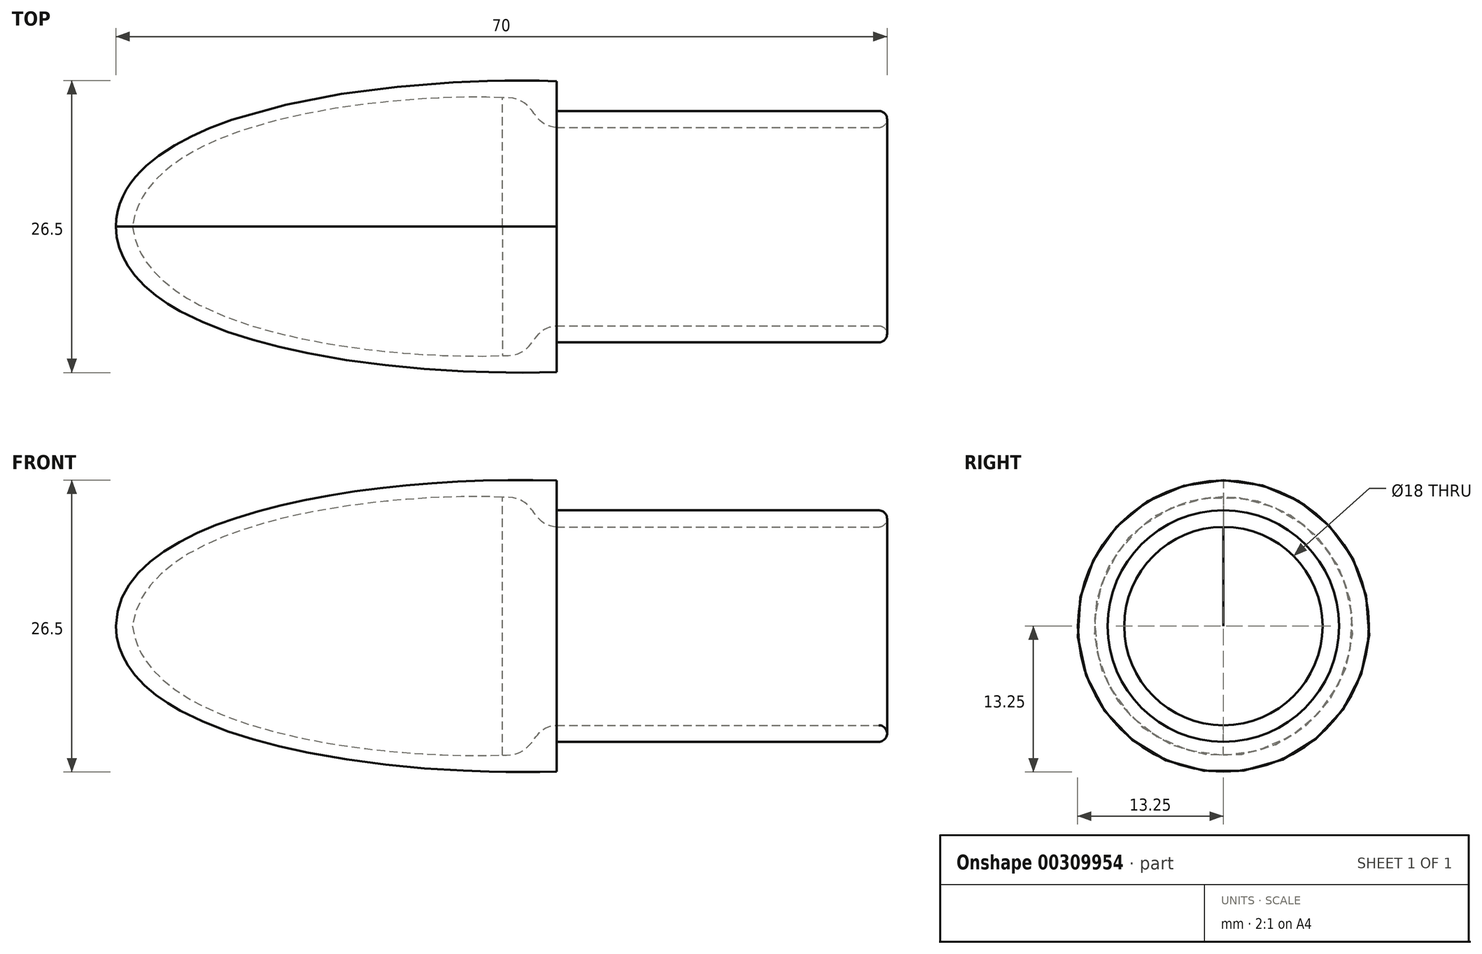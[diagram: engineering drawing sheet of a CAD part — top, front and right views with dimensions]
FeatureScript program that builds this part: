
annotation { "Feature Type Name" : "Feature", "Feature Type Description" : "" }
export const myFeature = defineFeature(function(context is Context, id is Id, definition is map)
    precondition{}
    {
        {
            var Q0;
            Q0=qCreatedBy(makeId("Front.planeOp"),FACE);
            var sketch = newSketch(context, id + "F0", { "sketchPlane" : qUnion([Q0])});
            skLineSegment(sketch, "E0", {"start": v(0, 10.5) * mm, "end": v(0, 13.2) * mm});
            skLineSegment(sketch, "E1", {"start": v(0, 10.5) * mm, "end": v(29.25, 10.5) * mm});
            skLineSegment(sketch, "E2", {"start": v(30, 9.75) * mm, "end": v(30, 9.75) * mm});
            skLineSegment(sketch, "E3", {"start": v(29.25, 9) * mm, "end": v(0, 9) * mm});
            skFitSpline(sketch, "E4", {"points": [v(0, 13.2) * mm, v(-40, 0) * mm], "startDerivative": vector(-48.79, 1.48) * mm, "endDerivative": vector(-0.4, -31.35) * mm});
            skLineSegment(sketch, "E5", {"start": v(-40, 0) * mm, "end": v(-38.5, 0) * mm});
            skLineSegment(sketch, "E6", {"start": v(0, 0) * mm, "end": v(-68.39, 0) * mm, "construction": true});
            skPoint(sketch, "E7.visualSharp", {"position": v(30, 10.5) * mm});
            skArc(sketch, "E7.filletArc", {"start": v(30, 9.75) * mm, "mid": v(29.78, 10.28) * mm, "end": v(29.25, 10.5) * mm});
            skFitSpline(sketch, "E8", {"points": [v(-4.92, 11.7) * mm, v(-38.5, 0) * mm], "startDerivative": vector(-22.78, 1.2) * mm, "endDerivative": vector(-3.98, -31.78) * mm});
            skFitSpline(sketch, "E9", {"points": [v(-4.92, 11.7) * mm, v(0, 9) * mm], "startDerivative": vector(9.56, 0.52) * mm, "endDerivative": vector(7.43, -0.43) * mm});
            skPoint(sketch, "E10.visualSharp", {"position": v(30, 9) * mm});
            skArc(sketch, "E10.filletArc", {"start": v(29.25, 9) * mm, "mid": v(29.78, 9.22) * mm, "end": v(30, 9.75) * mm});
            skSolve(sketch);
        }
        {
            var Q0;
            Q0 = qSketchRegion(id + "F0", true);
            var Q1;
            Q1=sQuery(id+"F0.wireOp",EDGE,"E6");
            revolve(context, id + "F1", {"entities" : qUnion([Q0]), "axis" : qUnion([Q1]), "revolveType" : RevolveType.FULL});
        }
    });
